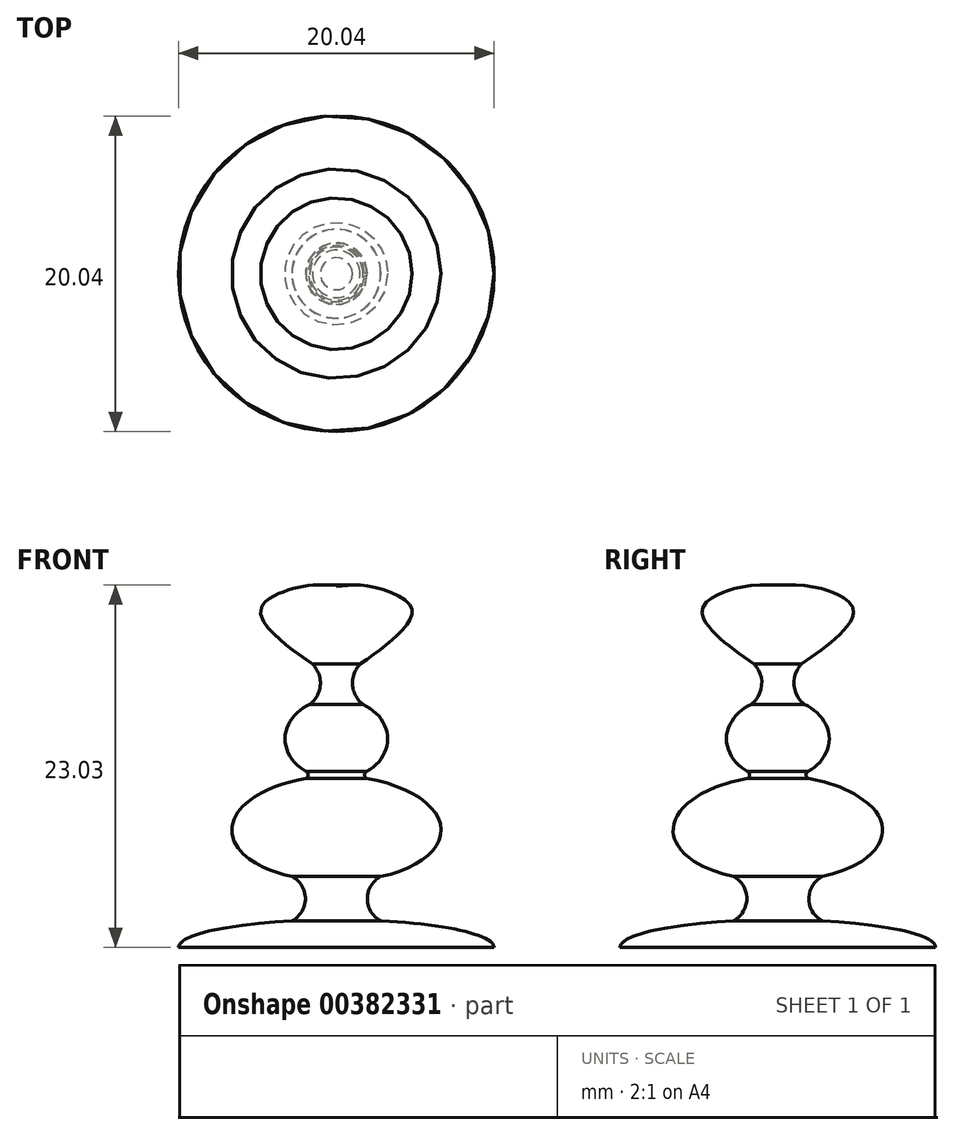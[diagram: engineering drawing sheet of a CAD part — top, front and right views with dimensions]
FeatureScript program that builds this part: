
annotation { "Feature Type Name" : "Feature", "Feature Type Description" : "" }
export const myFeature = defineFeature(function(context is Context, id is Id, definition is map)
    precondition{}
    {
        {
            var Q0;
            Q0=qCreatedBy(makeId("Front.planeOp"),FACE);
            var sketch = newSketch(context, id + "F0", { "sketchPlane" : qUnion([Q0])});
            skEllipticalArc(sketch, "E0", {});
            skEllipticalArc(sketch, "E1", {});
            skEllipticalArc(sketch, "E2", {});
            skArc(sketch, "E3", {"start": v(1.5, 8.53) * mm, "mid": v(1.02, 7.2) * mm, "end": v(1.69, 5.97) * mm});
            skArc(sketch, "E4", {"start": v(1.92, 1.7) * mm, "mid": v(1.8, 1.48) * mm, "end": v(1.93, 1.27) * mm});
            skArc(sketch, "E5", {"start": v(2.82, -4.97) * mm, "mid": v(1.97, -6.38) * mm, "end": v(2.83, -7.78) * mm});
            skLineSegment(sketch, "E6", {"start": v(0, 13.46) * mm, "end": v(0, -11.64) * mm});
            skPoint(sketch, "E6.endSnap0", {"position": v(0, -11.25) * mm});
            skLineSegment(sketch, "E7", {"start": v(0, -9.48) * mm, "end": v(10.02, -9.48) * mm});
            skPoint(sketch, "E7.endSnap0", {"position": v(10.02, -9.48) * mm});
            skPoint(sketch, "E8.orphan", {"position": v(11.31, -9.48) * mm});
            skFitSpline(sketch, "E9", {"points": [v(1.5, 8.53) * mm, v(4.1, 10.57) * mm, v(4.75, 12.15) * mm, v(2.13, 13.46) * mm, v(0, 13.46) * mm], "startDerivative": vector(9.82, 6.83) * mm, "endDerivative": vector(-8.22, -1) * mm});
            const initialGuessF0  = {"E0": [0, -0.009478879234426116, 1, 0, 0.010022994581408033, 0.001766548540903922, 0, 1.2847515187519276], "E1": [0, -0.0018853072341463047, 0.9995705631396107, -0.029303400907773423, 0.006652967126485593, 0.003335786041978901, 5.164183644601306, 1.291262574658104], "E2": [0, 0.0037703954419413648, 1, 0, 0.003264200262553529, 0.002565681737332578, 5.341905469167101, 1.0272761205556598]};
            skSetInitialGuess(sketch, initialGuessF0);
            skSolve(sketch);
        }
        {
            var Q0;
            Q0=makeQuery(id+"F0.imprint","IMPRINT",FACE,{"disambiguationData":[TD([[makeQuery(id+"F0.imprint","IMPRINT",EDGE,{"derivedFrom":sQuery(id+"F0.wireOp",EDGE,"E0")}),1.0]])]});
            var Q1;
            Q1=sQuery(id+"F0.wireOp",EDGE,"E6");
            revolve(context, id + "F1", {"entities" : qUnion([Q0]), "axis" : qUnion([Q1]), "revolveType" : RevolveType.FULL});
        }
    });
